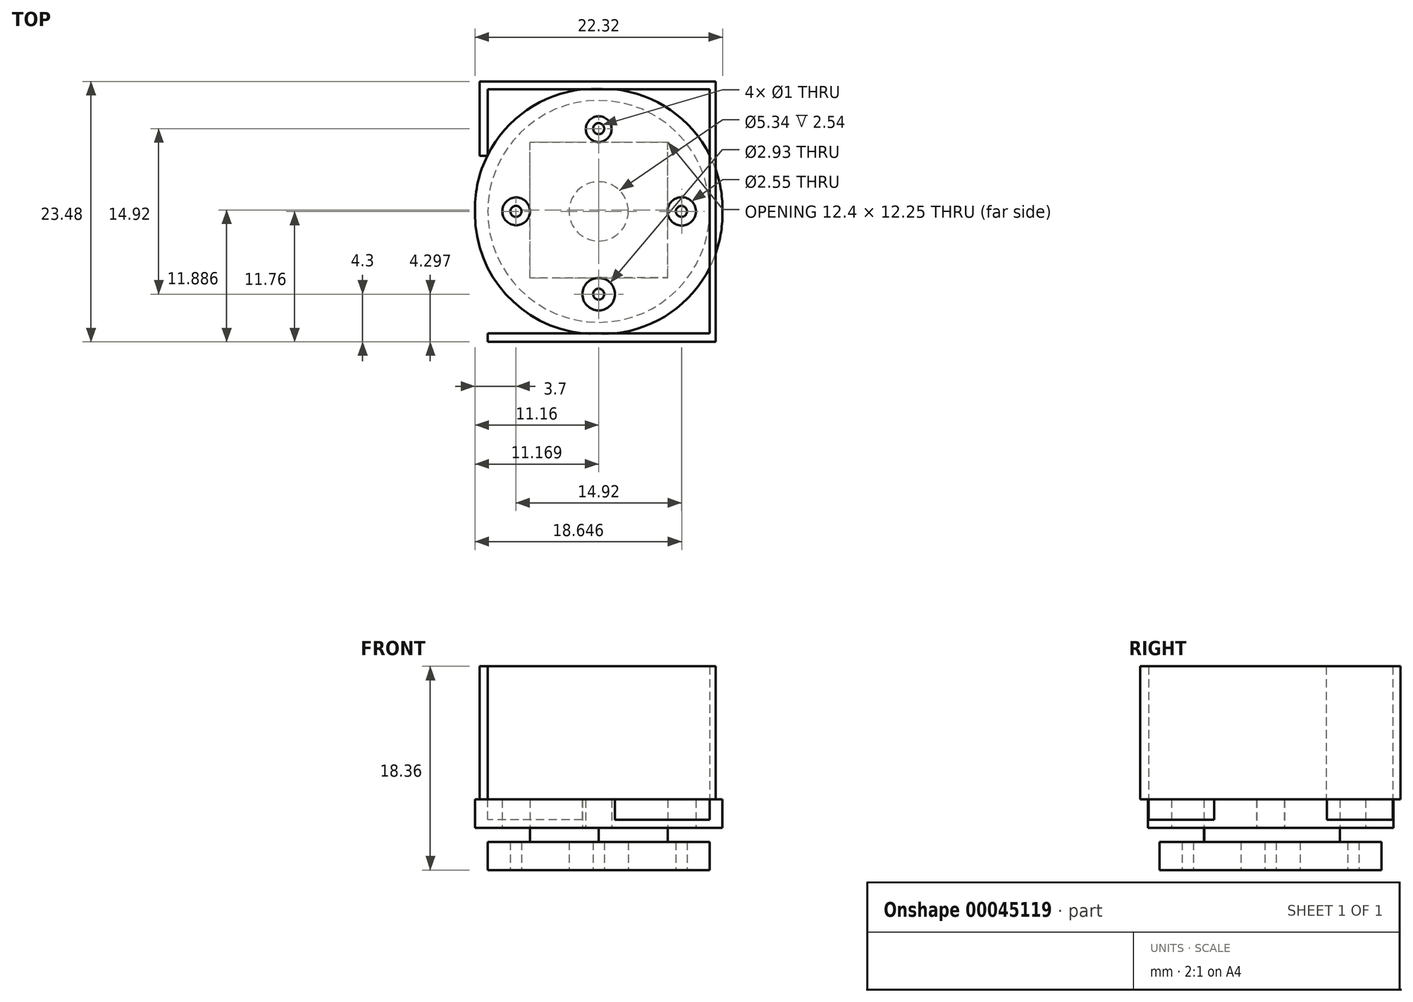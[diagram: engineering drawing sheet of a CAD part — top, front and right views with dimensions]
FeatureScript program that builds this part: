
annotation { "Feature Type Name" : "Feature", "Feature Type Description" : "" }
export const myFeature = defineFeature(function(context is Context, id is Id, definition is map)
    precondition{}
    {
        {
            var Q0;
            Q0=qCreatedBy(makeId("Top.planeOp"),FACE);
            var sketch = newSketch(context, id + "F0", { "sketchPlane" : qUnion([Q0])});
            skCircle(sketch, "E0", {"center": v(0, 0) * mm, "radius": 10 * mm});
            skLineSegment(sketch, "E1", {"start": v(0, 10) * mm, "end": v(0, 7.46) * mm});
            skLineSegment(sketch, "E2", {"start": v(-10, 0) * mm, "end": v(-7.46, 0) * mm});
            skLineSegment(sketch, "E3", {"start": v(0, -10) * mm, "end": v(0, -7.46) * mm});
            skLineSegment(sketch, "E4", {"start": v(10, 0) * mm, "end": v(7.46, 0) * mm});
            skCircle(sketch, "E5", {"center": v(-7.46, 0) * mm, "radius": 0.5 * mm});
            skCircle(sketch, "E6", {"center": v(0, 7.46) * mm, "radius": 0.5 * mm});
            skCircle(sketch, "E7", {"center": v(7.46, 0) * mm, "radius": 0.5 * mm});
            skCircle(sketch, "E8", {"center": v(0, -7.46) * mm, "radius": 0.5 * mm});
            skCircle(sketch, "E9", {"center": v(0, 0) * mm, "radius": 2.67 * mm});
            skSolve(sketch);
        }
        {
            var Q0;
            Q0=makeQuery(id+"F0.imprint","IMPRINT",FACE,{"disambiguationData":[TD([[makeQuery(id+"F0.imprint","IMPRINT",EDGE,{"derivedFrom":sQuery(id+"F0.wireOp",EDGE,"E5")}),-1.0]])]});
            extrude(context, id + "F1", {"entities" : qUnion([Q0]), "depth" : 2.54 * mm});
        }
        {
            var Q0;
            Q0=makeQuery(id+"F1.opExtrude","CAP_FACE",FACE,{"disambiguationData":[OSD([sQuery(id+"F0.wireOp",EDGE,"E0"),sQuery(id+"F0.wireOp",EDGE,"E5"),sQuery(id+"F0.wireOp",EDGE,"E6"),sQuery(id+"F0.wireOp",EDGE,"E7"),sQuery(id+"F0.wireOp",EDGE,"E8"),sQuery(id+"F0.wireOp",EDGE,"E9")])],"isStart":false});
            var sketch = newSketch(context, id + "F2", { "sketchPlane" : qUnion([Q0])});
            skLineSegment(sketch, "E10.bottom", {"start": v(0, 0) * mm, "end": v(-6.19, 0) * mm});
            skLineSegment(sketch, "E10.top", {"start": v(0, 6.21) * mm, "end": v(-6.19, 6.21) * mm});
            skLineSegment(sketch, "E10.left", {"start": v(0, 0) * mm, "end": v(0, 6.21) * mm});
            skLineSegment(sketch, "E10.right", {"start": v(-6.19, 0) * mm, "end": v(-6.19, 6.21) * mm});
            skLineSegment(sketch, "E11.top", {"start": v(0, -6) * mm, "end": v(-6.19, -6) * mm});
            skLineSegment(sketch, "E11.left", {"start": v(0, 0) * mm, "end": v(0, -6) * mm});
            skLineSegment(sketch, "E11.right", {"start": v(-6.19, 0) * mm, "end": v(-6.19, -6) * mm});
            skLineSegment(sketch, "E12.bottom", {"start": v(0, 0) * mm, "end": v(6.2, 0) * mm});
            skLineSegment(sketch, "E12.top", {"start": v(0, -5.96) * mm, "end": v(6.2, -5.96) * mm});
            skLineSegment(sketch, "E12.left", {"start": v(0, 0) * mm, "end": v(0, -5.96) * mm});
            skLineSegment(sketch, "E12.right", {"start": v(6.2, 0) * mm, "end": v(6.2, -5.96) * mm});
            skLineSegment(sketch, "E13.top", {"start": v(0, 6.25) * mm, "end": v(6.2, 6.25) * mm});
            skLineSegment(sketch, "E13.left", {"start": v(0, 0) * mm, "end": v(0, 6.25) * mm});
            skLineSegment(sketch, "E13.right", {"start": v(6.2, 0) * mm, "end": v(6.2, 6.25) * mm});
            skSolve(sketch);
        }
        {
            var Q0;
            {var subQ5=sQuery(id+"F2.wireOp",EDGE,"E10.top");Q0=makeQuery(id+"F2.imprint","IMPRINT",FACE,{"disambiguationData":[TD([[makeQuery(id+"F2.imprint","IMPRINT",EDGE,{"derivedFrom":subQ5}),1.0]])]});}
            var Q1;
            {var subQ6=sQuery(id+"F2.wireOp",EDGE,"E13.top");Q1=makeQuery(id+"F2.imprint","IMPRINT",FACE,{"disambiguationData":[TD([[makeQuery(id+"F2.imprint","IMPRINT",EDGE,{"derivedFrom":subQ6}),-1.0]])]});}
            var Q2;
            Q2=makeQuery(id+"F2.imprint","IMPRINT",FACE,{"disambiguationData":[TD([[makeQuery(id+"F2.imprint","IMPRINT",EDGE,{"derivedFrom":sQuery(id+"F2.wireOp",EDGE,"E11.top")}),-1.0]])]});
            var Q3;
            {var subQ5=sQuery(id+"F2.wireOp",EDGE,"E12.top");Q3=makeQuery(id+"F2.imprint","IMPRINT",FACE,{"disambiguationData":[TD([[makeQuery(id+"F2.imprint","IMPRINT",EDGE,{"derivedFrom":subQ5}),1.0]])]});}
            var Q4;
            {var subQ0=makeQuery(id+"F1.opExtrude","CAP_EDGE",EDGE,{"disambiguationData":[OSD([sQuery(id+"F0.wireOp",EDGE,"E9")])],"isStart":false});var subQ3=sQuery(id+"F2.wireOp",EDGE,"E12.left");var subQ4=makeQuery(id+"F2.imprint","INTERSECT",VERTEX,{"derivedFrom":[subQ0,subQ3]});Q4=makeQuery(id+"F2.imprint","IMPRINT",FACE,{"disambiguationData":[TD([[makeQuery(id+"F2.imprint","IMPRINT",EDGE,{"disambiguationData":[TD([[subQ4,-1.0]])],"derivedFrom":subQ0}),1.0]])]});}
            var Q5;
            {var subQ0=makeQuery(id+"F1.opExtrude","CAP_EDGE",EDGE,{"disambiguationData":[OSD([sQuery(id+"F0.wireOp",EDGE,"E9")])],"isStart":false});var subQ3=sQuery(id+"F2.wireOp",EDGE,"E10.bottom");var subQ4=makeQuery(id+"F2.imprint","INTERSECT",VERTEX,{"derivedFrom":[subQ0,subQ3]});Q5=makeQuery(id+"F2.imprint","IMPRINT",FACE,{"disambiguationData":[TD([[makeQuery(id+"F2.imprint","IMPRINT",EDGE,{"disambiguationData":[TD([[subQ4,-1.0]])],"derivedFrom":subQ0}),1.0]])]});}
            var Q6;
            {var subQ1=makeQuery(id+"F1.opExtrude","CAP_EDGE",EDGE,{"disambiguationData":[OSD([sQuery(id+"F0.wireOp",EDGE,"E9")])],"isStart":false});var subQ3=sQuery(id+"F2.wireOp",EDGE,"E10.bottom");var subQ5=makeQuery(id+"F2.imprint","INTERSECT",VERTEX,{"derivedFrom":[subQ1,subQ3]});Q6=makeQuery(id+"F2.imprint","IMPRINT",FACE,{"disambiguationData":[TD([[makeQuery(id+"F2.imprint","IMPRINT",EDGE,{"disambiguationData":[TD([[subQ5,1.0]])],"derivedFrom":subQ1}),1.0]])]});}
            var Q7;
            {var subQ1=makeQuery(id+"F1.opExtrude","CAP_EDGE",EDGE,{"disambiguationData":[OSD([sQuery(id+"F0.wireOp",EDGE,"E9")])],"isStart":false});var subQ3=sQuery(id+"F2.wireOp",EDGE,"E12.bottom");var subQ5=makeQuery(id+"F2.imprint","INTERSECT",VERTEX,{"derivedFrom":[subQ1,subQ3]});Q7=makeQuery(id+"F2.imprint","IMPRINT",FACE,{"disambiguationData":[TD([[makeQuery(id+"F2.imprint","IMPRINT",EDGE,{"disambiguationData":[TD([[subQ5,-1.0]])],"derivedFrom":subQ1}),1.0]])]});}
            extrude(context, id + "F3", {"entities" : qUnion([Q0, Q1, Q2, Q3, Q4, Q5, Q6, Q7]), "operationType" : NewBodyOperationType.ADD, "depth" : 1.27 * mm});
        }
        {
            var Q0;
            Q0=makeQuery(id+"F3.opExtrude","CAP_FACE",FACE,{"disambiguationData":[OSD([sQuery(id+"F2.wireOp",EDGE,"E10.top"),sQuery(id+"F2.wireOp",EDGE,"E10.right"),sQuery(id+"F2.wireOp",EDGE,"E11.top"),sQuery(id+"F2.wireOp",EDGE,"E11.left"),sQuery(id+"F2.wireOp",EDGE,"E11.right"),sQuery(id+"F2.wireOp",EDGE,"E12.top"),sQuery(id+"F2.wireOp",EDGE,"E12.right"),sQuery(id+"F2.wireOp",EDGE,"E13.top"),sQuery(id+"F2.wireOp",EDGE,"E13.left"),sQuery(id+"F2.wireOp",EDGE,"E13.right")])],"isStart":false});
            var sketch = newSketch(context, id + "F4", { "sketchPlane" : qUnion([Q0])});
            skLineSegment(sketch, "E14.rect.bottom", {"start": v(11.16, 11.06) * mm, "end": v(-11.16, 11.06) * mm});
            skLineSegment(sketch, "E14.rect.top", {"start": v(11.16, -11.06) * mm, "end": v(-11.16, -11.06) * mm});
            skLineSegment(sketch, "E14.rect.left", {"start": v(11.16, 11.06) * mm, "end": v(11.16, -11.06) * mm});
            skLineSegment(sketch, "E14.rect.right", {"start": v(-11.16, 11.06) * mm, "end": v(-11.16, -11.06) * mm});
            skPoint(sketch, "E14.rect.middle", {"position": v(0, 0) * mm});
            skCircle(sketch, "E15", {"center": v(-7.44, 0) * mm, "radius": 1.25 * mm});
            skCircle(sketch, "E16", {"center": v(7.49, 0) * mm, "radius": 1.28 * mm});
            skCircle(sketch, "E17", {"center": v(0, 7.41) * mm, "radius": 1.16 * mm});
            skCircle(sketch, "E18", {"center": v(0, -7.46) * mm, "radius": 1.46 * mm});
            skSolve(sketch);
        }
        {
            var Q0;
            Q0=makeQuery(id+"F4.imprint","IMPRINT",FACE,{"disambiguationData":[TD([[makeQuery(id+"F4.imprint","IMPRINT",EDGE,{"derivedFrom":sQuery(id+"F4.wireOp",EDGE,"E14.rect.bottom")}),1.0]])]});
            var Q1;
            {var subQ7=makeQuery(id+"F3.opExtrude","CAP_EDGE",EDGE,{"disambiguationData":[OSD([sQuery(id+"F2.wireOp",EDGE,"E10.top")])],"isStart":false});Q1=makeQuery(id+"F4.imprint","IMPRINT",FACE,{"disambiguationData":[TD([[makeQuery(id+"F4.imprint","IMPRINT",EDGE,{"derivedFrom":subQ7}),1.0]])]});}
            extrude(context, id + "F5", {"entities" : qUnion([Q0, Q1]), "operationType" : NewBodyOperationType.ADD, "depth" : 2.55 * mm});
        }
        {
            var Q0;
            Q0=makeQuery(id+"F5.opExtrude","SWEPT_EDGE",EDGE,{"disambiguationData":[OSD([sQuery(id+"F4.wireOp",EDGE,"E14.rect.top"),sQuery(id+"F4.wireOp",EDGE,"E14.rect.right")])]});
            var Q1;
            Q1=makeQuery(id+"F5.opExtrude","SWEPT_EDGE",EDGE,{"disambiguationData":[OSD([sQuery(id+"F4.wireOp",EDGE,"E14.rect.top"),sQuery(id+"F4.wireOp",EDGE,"E14.rect.left")])]});
            var Q2;
            Q2=makeQuery(id+"F5.opExtrude","SWEPT_EDGE",EDGE,{"disambiguationData":[OSD([sQuery(id+"F4.wireOp",EDGE,"E14.rect.bottom"),sQuery(id+"F4.wireOp",EDGE,"E14.rect.left")])]});
            var Q3;
            Q3=makeQuery(id+"F5.opExtrude","SWEPT_EDGE",EDGE,{"disambiguationData":[OSD([sQuery(id+"F4.wireOp",EDGE,"E14.rect.bottom"),sQuery(id+"F4.wireOp",EDGE,"E14.rect.right")])]});
            fillet(context, id + "F6", {"entities" : qUnion([Q0, Q1, Q2, Q3]), "radius" : 10.86 * mm, "tangentPropagation" : true, "allowEdgeOverflow" : false});
        }
        {
            var Q0;
            Q0=makeQuery(id+"F5.opExtrude","CAP_FACE",FACE,{"disambiguationData":[OSD([sQuery(id+"F4.wireOp",EDGE,"E14.rect.bottom"),sQuery(id+"F4.wireOp",EDGE,"E14.rect.top"),sQuery(id+"F4.wireOp",EDGE,"E14.rect.left"),sQuery(id+"F4.wireOp",EDGE,"E14.rect.right"),sQuery(id+"F4.wireOp",EDGE,"E15"),sQuery(id+"F4.wireOp",EDGE,"E16"),sQuery(id+"F4.wireOp",EDGE,"E17"),sQuery(id+"F4.wireOp",EDGE,"E18")])],"isStart":false});
            var sketch = newSketch(context, id + "F7", { "sketchPlane" : qUnion([Q0])});
            skLineSegment(sketch, "E19.rect.bottom", {"start": v(10, 11) * mm, "end": v(-10, 11) * mm});
            skLineSegment(sketch, "E19.rect.top", {"start": v(10, -11) * mm, "end": v(-10, -11) * mm});
            skLineSegment(sketch, "E19.rect.left", {"start": v(10, 11) * mm, "end": v(10, -11) * mm});
            skPoint(sketch, "E19.rect.middle", {"position": v(0, 0) * mm});
            skLineSegment(sketch, "E20", {"start": v(-10, 11) * mm, "end": v(-10, 5) * mm});
            skLineSegment(sketch, "E21", {"start": v(-10, 5) * mm, "end": v(-10.73, 5) * mm});
            skLineSegment(sketch, "E22", {"start": v(-10.73, 5) * mm, "end": v(-10.73, 11.72) * mm});
            skLineSegment(sketch, "E23", {"start": v(-10.73, 11.72) * mm, "end": v(10.54, 11.72) * mm});
            skLineSegment(sketch, "E24", {"start": v(10.54, 11.72) * mm, "end": v(10.54, -11.76) * mm});
            skLineSegment(sketch, "E25", {"start": v(10.54, -11.76) * mm, "end": v(-10, -11.76) * mm});
            skLineSegment(sketch, "E26", {"start": v(-10, -11.76) * mm, "end": v(-10, -11) * mm});
            skSolve(sketch);
        }
        {
            var Q0;
            Q0 = qSketchRegion(id + "F7", true);
            extrude(context, id + "F8", {"entities" : qUnion([Q0]), "operationType" : NewBodyOperationType.ADD, "depth" : 12 * mm});
        }
        {
            var Q0;
            {var subQ3=sQuery(id+"F7.wireOp",EDGE,"E19.rect.left");var subQ5=sQuery(id+"F7.wireOp",EDGE,"E19.rect.bottom");var subQ7=makeQuery(id+"F7.imprint","INTERSECT",VERTEX,{"derivedFrom":[subQ5,subQ3]});Q0=makeQuery(id+"F7.imprint","IMPRINT",FACE,{"disambiguationData":[TD([[makeQuery(id+"F7.imprint","IMPRINT",EDGE,{"disambiguationData":[TD([[subQ7,-1.0]])],"derivedFrom":subQ5}),1.0]])]});}
            var Q1;
            {var subQ3=sQuery(id+"F7.wireOp",EDGE,"E19.rect.left");var subQ5=sQuery(id+"F7.wireOp",EDGE,"E19.rect.top");var subQ7=makeQuery(id+"F7.imprint","INTERSECT",VERTEX,{"derivedFrom":[subQ5,subQ3]});Q1=makeQuery(id+"F7.imprint","IMPRINT",FACE,{"disambiguationData":[TD([[makeQuery(id+"F7.imprint","IMPRINT",EDGE,{"disambiguationData":[TD([[subQ7,-1.0]])],"derivedFrom":subQ5}),-1.0]])]});}
            var Q2;
            {var subQ3=sQuery(id+"F7.wireOp",EDGE,"E20");var subQ5=sQuery(id+"F7.wireOp",EDGE,"E19.rect.bottom");var subQ7=makeQuery(id+"F7.imprint","INTERSECT",VERTEX,{"derivedFrom":[subQ5,subQ3]});Q2=makeQuery(id+"F7.imprint","IMPRINT",FACE,{"disambiguationData":[TD([[makeQuery(id+"F7.imprint","IMPRINT",EDGE,{"disambiguationData":[TD([[subQ7,1.0]])],"derivedFrom":subQ5}),1.0]])]});}
            extrude(context, id + "F9", {"entities" : qUnion([Q0, Q1, Q2]), "oppositeDirection" : true, "depth" : 1.83 * mm});
        }
    });
